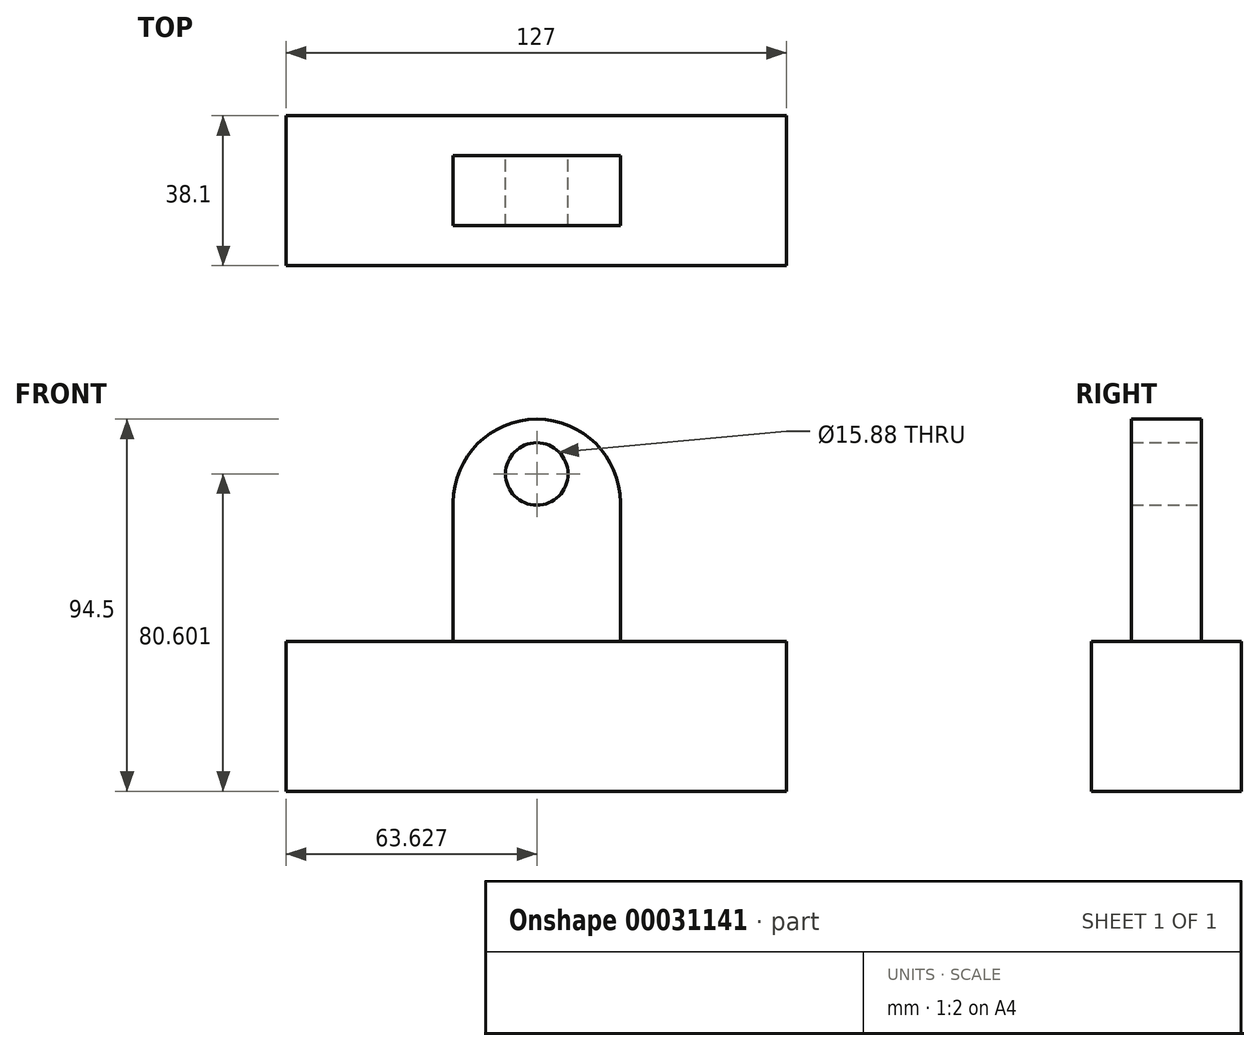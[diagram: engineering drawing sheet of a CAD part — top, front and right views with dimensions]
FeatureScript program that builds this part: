
annotation { "Feature Type Name" : "Feature", "Feature Type Description" : "" }
export const myFeature = defineFeature(function(context is Context, id is Id, definition is map)
    precondition{}
    {
        {
            var Q0;
            Q0=qCreatedBy(makeId("Front.planeOp"),FACE);
            var sketch = newSketch(context, id + "F0", { "sketchPlane" : qUnion([Q0])});
            skLineSegment(sketch, "E0.bottom", {"start": v(0, 0) * mm, "end": v(127, 0) * mm});
            skLineSegment(sketch, "E0.top", {"start": v(0, -38.1) * mm, "end": v(127, -38.1) * mm});
            skLineSegment(sketch, "E0.left", {"start": v(0, 0) * mm, "end": v(0, -38.1) * mm});
            skLineSegment(sketch, "E0.right", {"start": v(127, 0) * mm, "end": v(127, -38.1) * mm});
            skLineSegment(sketch, "E1.bottom", {"start": v(42.42, 35.19) * mm, "end": v(84.84, 35.19) * mm});
            skLineSegment(sketch, "E1.top", {"start": v(42.42, 0) * mm, "end": v(84.84, 0) * mm});
            skLineSegment(sketch, "E1.left", {"start": v(42.42, 35.19) * mm, "end": v(42.42, 0) * mm});
            skLineSegment(sketch, "E1.right", {"start": v(84.84, 35.19) * mm, "end": v(84.84, 0) * mm});
            skArc(sketch, "E2", {"start": v(84.84, 35.19) * mm, "mid": v(63.63, 56.4) * mm, "end": v(42.42, 35.19) * mm});
            skCircle(sketch, "E3", {"center": v(63.63, 42.5) * mm, "radius": 7.94 * mm});
            skSolve(sketch);
        }
        {
            var Q0;
            Q0=makeQuery(id+"F0.imprint","IMPRINT",FACE,{"disambiguationData":[TD([[makeQuery(id+"F0.imprint","IMPRINT",EDGE,{"derivedFrom":sQuery(id+"F0.wireOp",EDGE,"E0.top")}),1.0]])]});
            extrude(context, id + "F1", {"entities" : qUnion([Q0]), "endBound" : BoundingType.SYMMETRIC, "oppositeDirection" : true, "depth" : 38.1 * mm});
        }
        {
            var Q0;
            Q0 = qSketchRegion(id + "F0", true);
            extrude(context, id + "F2", {"entities" : qUnion([Q0]), "operationType" : NewBodyOperationType.ADD, "endBound" : BoundingType.SYMMETRIC, "depth" : 17.78 * mm});
        }
    });
